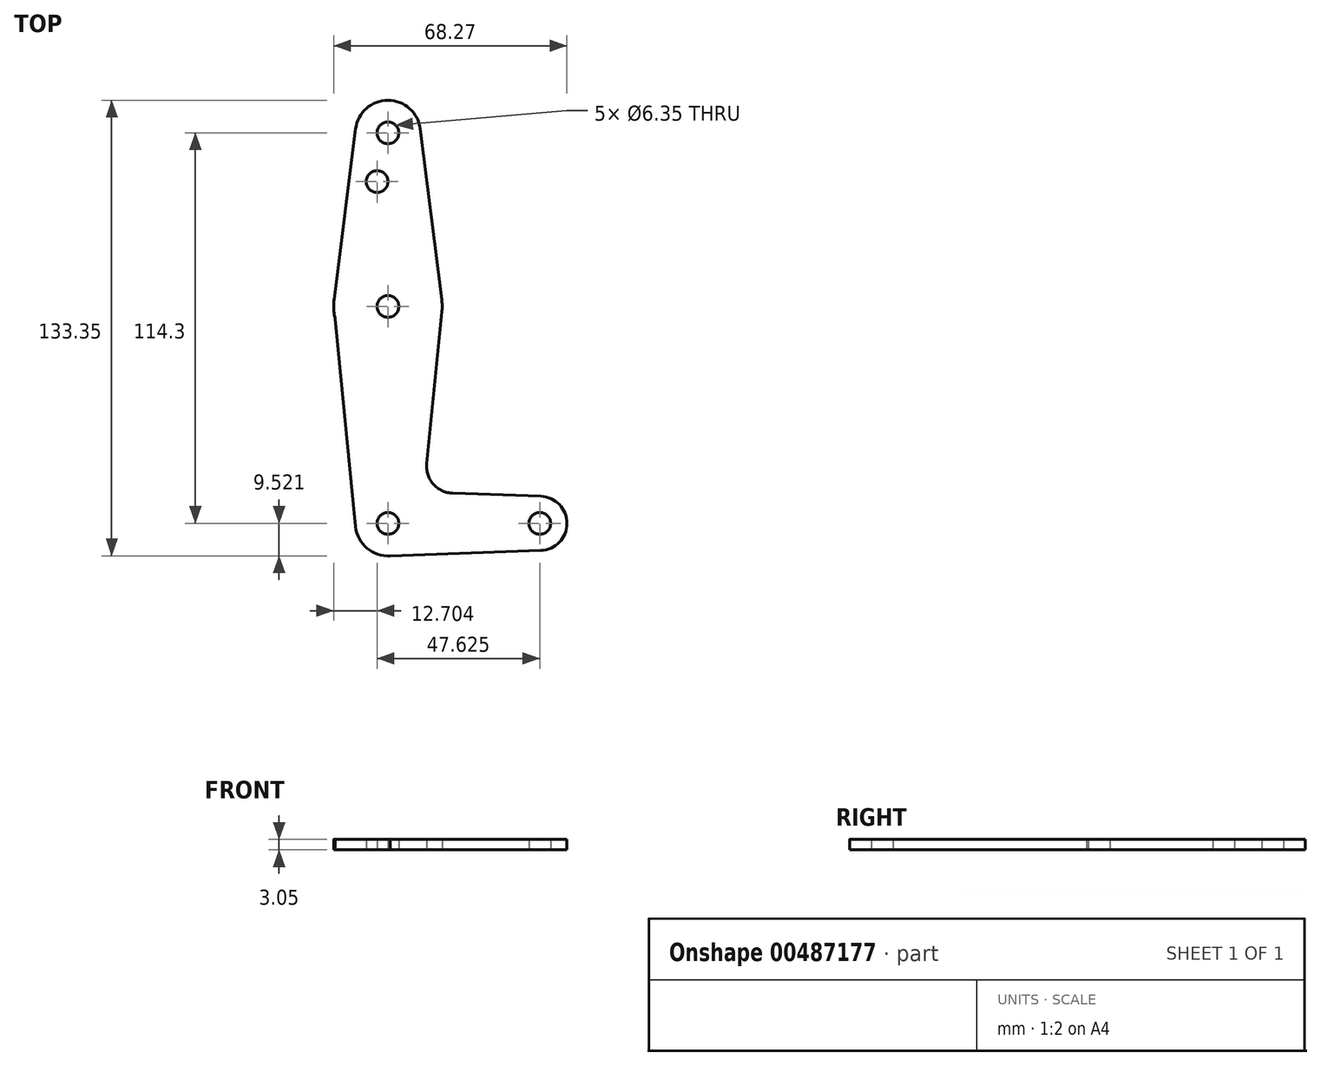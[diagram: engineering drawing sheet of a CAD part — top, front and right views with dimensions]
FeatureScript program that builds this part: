
annotation { "Feature Type Name" : "Feature", "Feature Type Description" : "" }
export const myFeature = defineFeature(function(context is Context, id is Id, definition is map)
    precondition{}
    {
        {
            var Q0;
            Q0=qCreatedBy(makeId("Top.planeOp"),FACE);
            var sketch = newSketch(context, id + "F0", { "sketchPlane" : qUnion([Q0])});
            skLineSegment(sketch, "E0", {"start": v(-40.64, 105.18) * mm, "end": v(-40.64, 13.48) * mm, "construction": true});
            skLineSegment(sketch, "E1", {"start": v(-40.64, 13.48) * mm, "end": v(-40.64, -9.12) * mm, "construction": true});
            skLineSegment(sketch, "E2", {"start": v(-40.64, -9.12) * mm, "end": v(3.8, -9.12) * mm, "construction": true});
            skCircle(sketch, "E3", {"center": v(-40.64, 105.18) * mm, "radius": 9.53 * mm});
            skCircle(sketch, "E4", {"center": v(-40.64, 54.38) * mm, "radius": 15.88 * mm});
            skCircle(sketch, "E5", {"center": v(-40.64, -9.12) * mm, "radius": 9.53 * mm});
            skCircle(sketch, "E6", {"center": v(3.8, -9.12) * mm, "radius": 7.94 * mm});
            skLineSegment(sketch, "E7", {"start": v(-50.1, 106.37) * mm, "end": v(-56.4, 56.37) * mm});
            skLineSegment(sketch, "E8", {"start": v(-31.2, 106.37) * mm, "end": v(-24.89, 56.34) * mm});
            skLineSegment(sketch, "E9", {"start": v(-56.1, 50.74) * mm, "end": v(-50.12, -10.05) * mm});
            skLineSegment(sketch, "E10", {"start": v(-24.85, 52.8) * mm, "end": v(-29.3, 8.43) * mm});
            skLineSegment(sketch, "E11", {"start": v(-21.66, -0.31) * mm, "end": v(4.08, -1.19) * mm});
            skLineSegment(sketch, "E12", {"start": v(-40.64, -18.64) * mm, "end": v(4.1, -17.05) * mm});
            skCircle(sketch, "E13", {"center": v(-43.82, 90.9) * mm, "radius": 3.18 * mm});
            skCircle(sketch, "E14", {"center": v(-40.64, 105.18) * mm, "radius": 3.18 * mm});
            skCircle(sketch, "E15", {"center": v(-40.64, -9.12) * mm, "radius": 3.18 * mm});
            skCircle(sketch, "E16", {"center": v(3.8, -9.12) * mm, "radius": 3.18 * mm});
            skCircle(sketch, "E17", {"center": v(-40.64, 54.38) * mm, "radius": 3.18 * mm});
            skArc(sketch, "E18.filletArc", {"start": v(-29.3, 8.43) * mm, "mid": v(-27.38, 2.4) * mm, "end": v(-21.66, -0.31) * mm});
            skSolve(sketch);
        }
        {
            var Q0;
            Q0 = qSketchRegion(id + "F0", true);
            extrude(context, id + "F1", {"entities" : qUnion([Q0]), "depth" : 3.05 * mm});
        }
    });
